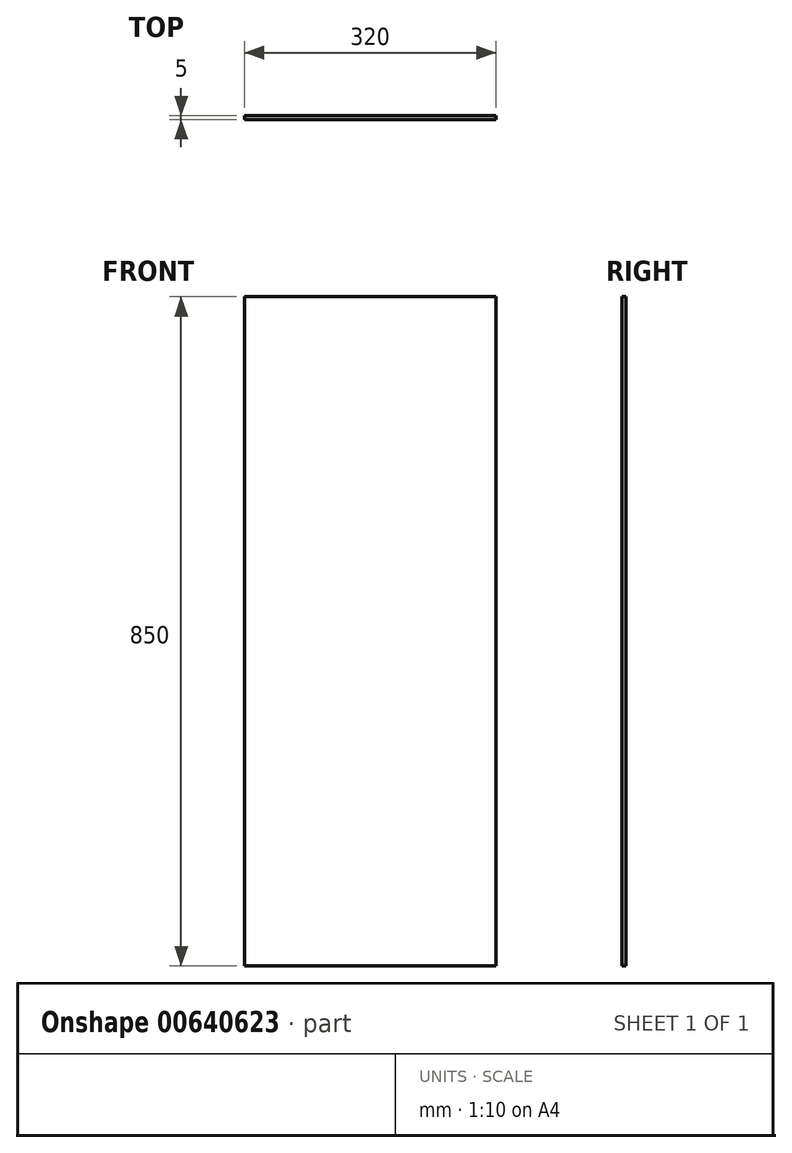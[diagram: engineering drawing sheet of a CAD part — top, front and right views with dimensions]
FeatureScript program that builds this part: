
annotation { "Feature Type Name" : "Feature", "Feature Type Description" : "" }
export const myFeature = defineFeature(function(context is Context, id is Id, definition is map)
    precondition{}
    {
        {
            var Q0;
            Q0=qCreatedBy(makeId("Front.planeOp"),FACE);
            var sketch = newSketch(context, id + "F0", { "sketchPlane" : qUnion([Q0])});
            skLineSegment(sketch, "E0.bottom", {"start": v(0, 0) * mm, "end": v(-320, 0) * mm});
            skLineSegment(sketch, "E0.top", {"start": v(0, 850) * mm, "end": v(-320, 850) * mm});
            skLineSegment(sketch, "E0.left", {"start": v(0, 0) * mm, "end": v(0, 850) * mm});
            skLineSegment(sketch, "E0.right", {"start": v(-320, 0) * mm, "end": v(-320, 850) * mm});
            skSolve(sketch);
        }
        {
            var Q0;
            Q0 = qSketchRegion(id + "F0", true);
            extrude(context, id + "F1", {"entities" : qUnion([Q0]), "depth" : 5 * mm, "offsetDistance" : 25 * mm});
        }
    });
